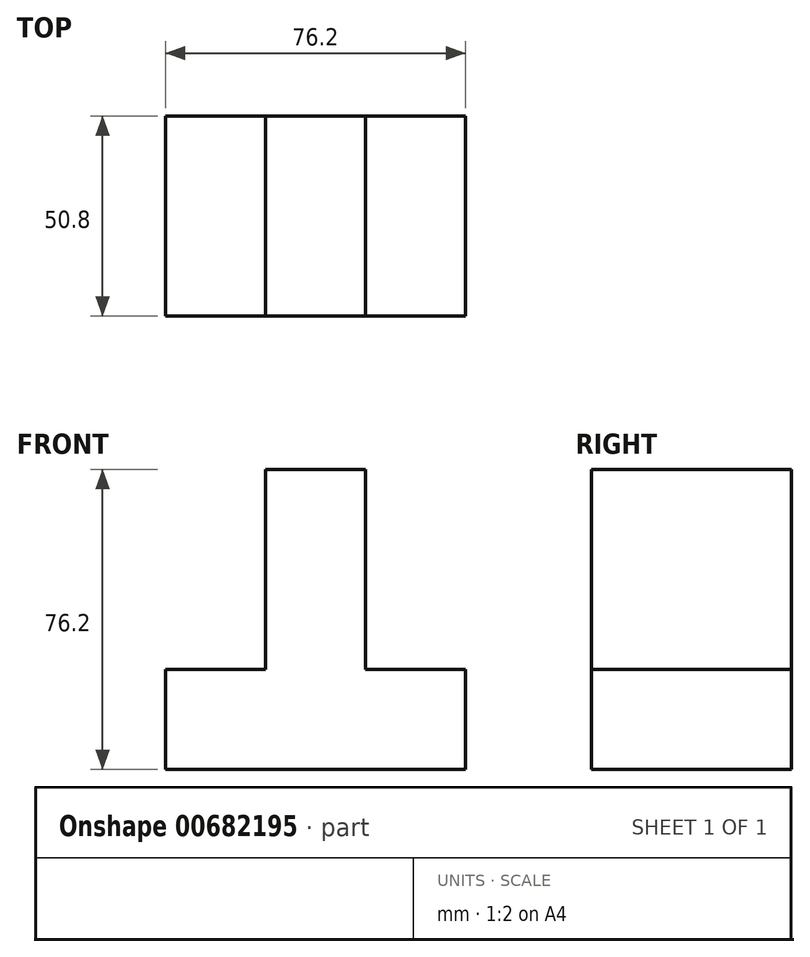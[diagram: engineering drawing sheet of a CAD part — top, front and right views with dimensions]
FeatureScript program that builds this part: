
annotation { "Feature Type Name" : "Feature", "Feature Type Description" : "" }
export const myFeature = defineFeature(function(context is Context, id is Id, definition is map)
    precondition{}
    {
        {
            var Q0;
            Q0=qCreatedBy(makeId("Front.planeOp"),FACE);
            var sketch = newSketch(context, id + "F0", { "sketchPlane" : qUnion([Q0])});
            skLineSegment(sketch, "E0", {"start": v(-28.36, -25.4) * mm, "end": v(47.84, -25.4) * mm});
            skLineSegment(sketch, "E1", {"start": v(-28.36, -25.4) * mm, "end": v(-28.36, 0) * mm});
            skLineSegment(sketch, "E2", {"start": v(-28.36, 0) * mm, "end": v(-2.96, 0) * mm});
            skLineSegment(sketch, "E3", {"start": v(-2.96, 0) * mm, "end": v(-2.96, 50.8) * mm});
            skLineSegment(sketch, "E4", {"start": v(47.84, -25.4) * mm, "end": v(47.84, 0) * mm});
            skLineSegment(sketch, "E5", {"start": v(47.84, 0) * mm, "end": v(22.44, 0) * mm});
            skLineSegment(sketch, "E6", {"start": v(22.44, 0) * mm, "end": v(22.44, 50.8) * mm});
            skLineSegment(sketch, "E7", {"start": v(22.44, 50.8) * mm, "end": v(-2.96, 50.8) * mm});
            skSolve(sketch);
        }
        {
            var Q0;
            Q0 = qSketchRegion(id + "F0", true);
            extrude(context, id + "F1", {"entities" : qUnion([Q0]), "depth" : 50.8 * mm, "offsetDistance" : 25.4 * mm});
        }
    });
